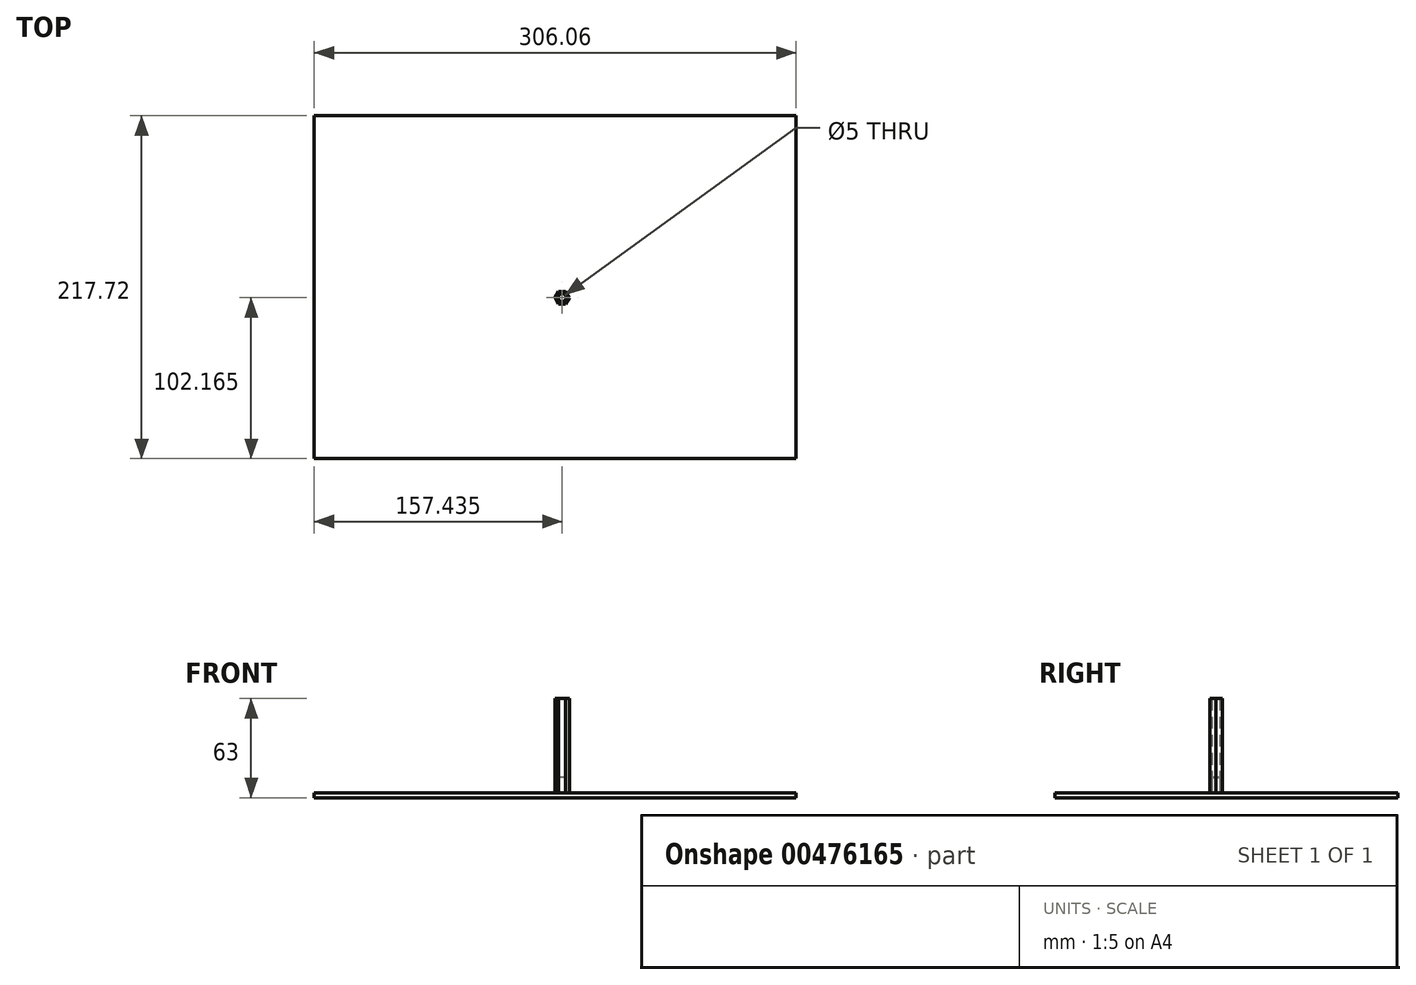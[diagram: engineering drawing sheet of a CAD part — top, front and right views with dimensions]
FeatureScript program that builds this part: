
annotation { "Feature Type Name" : "Feature", "Feature Type Description" : "" }
export const myFeature = defineFeature(function(context is Context, id is Id, definition is map)
    precondition{}
    {
        {
            var Q0;
            Q0=qCreatedBy(makeId("Top.planeOp"),FACE);
            var sketch = newSketch(context, id + "F0", { "sketchPlane" : qUnion([Q0])});
            skLineSegment(sketch, "E0.bottom", {"start": v(153.03, 108.86) * mm, "end": v(-153.03, 108.86) * mm});
            skLineSegment(sketch, "E0.top", {"start": v(153.03, -108.86) * mm, "end": v(-153.03, -108.86) * mm});
            skLineSegment(sketch, "E0.left", {"start": v(153.03, 108.86) * mm, "end": v(153.03, -108.86) * mm});
            skLineSegment(sketch, "E0.right", {"start": v(-153.03, 108.86) * mm, "end": v(-153.03, -108.86) * mm});
            skPoint(sketch, "E0.middle", {"position": v(0, 0) * mm});
            skSolve(sketch);
        }
        {
            var Q0;
            Q0 = qSketchRegion(id + "F0", true);
            extrude(context, id + "F1", {"entities" : qUnion([Q0]), "depth" : 3 * mm});
        }
        {
            var Q0;
            Q0=makeQuery(id+"F1.opExtrude","CAP_FACE",FACE,{"disambiguationData":[OSD([sQuery(id+"F0.wireOp",EDGE,"E0.bottom"),sQuery(id+"F0.wireOp",EDGE,"E0.top"),sQuery(id+"F0.wireOp",EDGE,"E0.left"),sQuery(id+"F0.wireOp",EDGE,"E0.right")])],"isStart":false});
            var sketch = newSketch(context, id + "F2", { "sketchPlane" : qUnion([Q0])});
            skCircle(sketch, "E1", {"center": v(4.4, -6.7) * mm, "radius": 2.5 * mm});
            skCircle(sketch, "E2.cCircle", {"center": v(4.4, -6.7) * mm, "radius": 4 * mm, "construction": true});
            skLineSegment(sketch, "E2.0", {"start": v(2.1, -2.7) * mm, "end": v(6.71, -2.7) * mm});
            skLineSegment(sketch, "E2.1", {"start": v(6.71, -2.7) * mm, "end": v(9.02, -6.7) * mm});
            skLineSegment(sketch, "E2.2", {"start": v(9.02, -6.7) * mm, "end": v(6.71, -10.7) * mm});
            skLineSegment(sketch, "E2.3", {"start": v(6.71, -10.7) * mm, "end": v(2.1, -10.7) * mm});
            skLineSegment(sketch, "E2.4", {"start": v(2.1, -10.7) * mm, "end": v(-0.21, -6.7) * mm});
            skLineSegment(sketch, "E2.5", {"start": v(-0.21, -6.7) * mm, "end": v(2.1, -2.7) * mm});
            skPoint(sketch, "E2.0.midPoint", {"position": v(4.4, -2.7) * mm});
            skSolve(sketch);
        }
        {
            var Q0;
            Q0=makeQuery(id+"F2.imprint","IMPRINT",FACE,{"disambiguationData":[TD([[makeQuery(id+"F2.imprint","IMPRINT",EDGE,{"derivedFrom":sQuery(id+"F2.wireOp",EDGE,"E1")}),1.0]])]});
            extrude(context, id + "F3", {"entities" : qUnion([Q0]), "operationType" : NewBodyOperationType.ADD, "depth" : 10 * mm});
        }
        {
            var Q0;
            Q0=makeQuery(id+"F2.imprint","IMPRINT",FACE,{"disambiguationData":[TD([[makeQuery(id+"F2.imprint","IMPRINT",EDGE,{"derivedFrom":sQuery(id+"F2.wireOp",EDGE,"E1")}),-1.0]])]});
            extrude(context, id + "F4", {"entities" : qUnion([Q0]), "depth" : 60 * mm});
        }
    });
